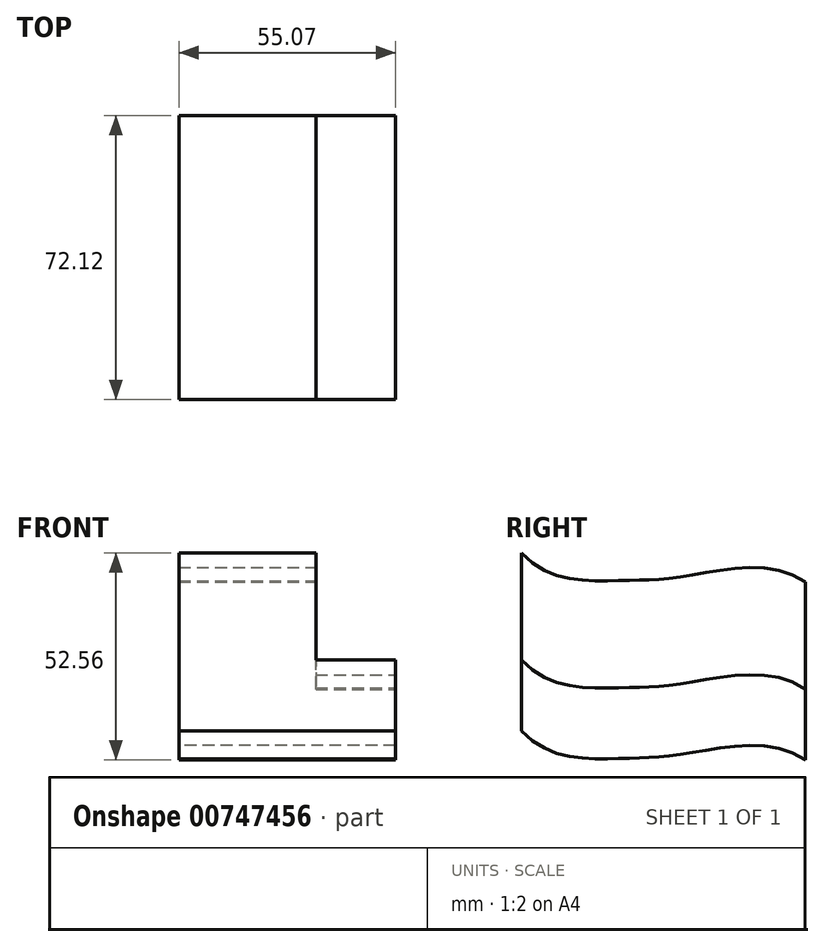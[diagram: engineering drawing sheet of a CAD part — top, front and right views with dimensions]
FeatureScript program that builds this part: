
annotation { "Feature Type Name" : "Feature", "Feature Type Description" : "" }
export const myFeature = defineFeature(function(context is Context, id is Id, definition is map)
    precondition{}
    {
        {
            var Q0;
            Q0=qCreatedBy(makeId("Front.planeOp"),FACE);
            var sketch = newSketch(context, id + "F0", { "sketchPlane" : qUnion([Q0])});
            skLineSegment(sketch, "E0.bottom", {"start": v(-55.07, 20.96) * mm, "end": v(-20.23, 20.96) * mm});
            skLineSegment(sketch, "E0.top", {"start": v(-55.07, -24.22) * mm, "end": v(-20.23, -24.22) * mm});
            skLineSegment(sketch, "E0.left", {"start": v(-55.07, 20.96) * mm, "end": v(-55.07, -24.22) * mm});
            skLineSegment(sketch, "E0.right", {"start": v(-20.23, 20.96) * mm, "end": v(-20.23, -6.26) * mm});
            skLineSegment(sketch, "E1.bottom", {"start": v(-20.23, -24.22) * mm, "end": v(0, -24.22) * mm});
            skLineSegment(sketch, "E1.top", {"start": v(-20.23, -6.26) * mm, "end": v(0, -6.26) * mm});
            skLineSegment(sketch, "E1.right", {"start": v(0, -24.22) * mm, "end": v(0, -6.26) * mm});
            skSolve(sketch);
        }
        {
            var Q0;
            Q0=qCreatedBy(makeId("Right.planeOp"),FACE);
            var sketch = newSketch(context, id + "F1", { "sketchPlane" : qUnion([Q0])});
            skFitSpline(sketch, "E2", {"points": [v(0, -24.22) * mm, v(-30.86, -22.75) * mm, v(-47.81, -23.86) * mm, v(-72.12, -16.84) * mm], "startDerivative": vector(-71.35, 49.96) * mm, "endDerivative": vector(-60.51, 67.05) * mm});
            skSolve(sketch);
        }
        {
            var Q0;
            Q0=makeQuery(id+"F0.imprint","IMPRINT",FACE,{"disambiguationData":[TD([[makeQuery(id+"F0.imprint","IMPRINT",EDGE,{"derivedFrom":sQuery(id+"F0.wireOp",EDGE,"E0.bottom")}),-1.0]])]});
            var Q1;
            Q1=sQuery(id+"F1.wireOp",EDGE,"E2");
            sweep(context, id + "F2", {"profiles" : qUnion([Q0]), "path" : qUnion([Q1]), "keepProfileOrientation" : true});
        }
    });
